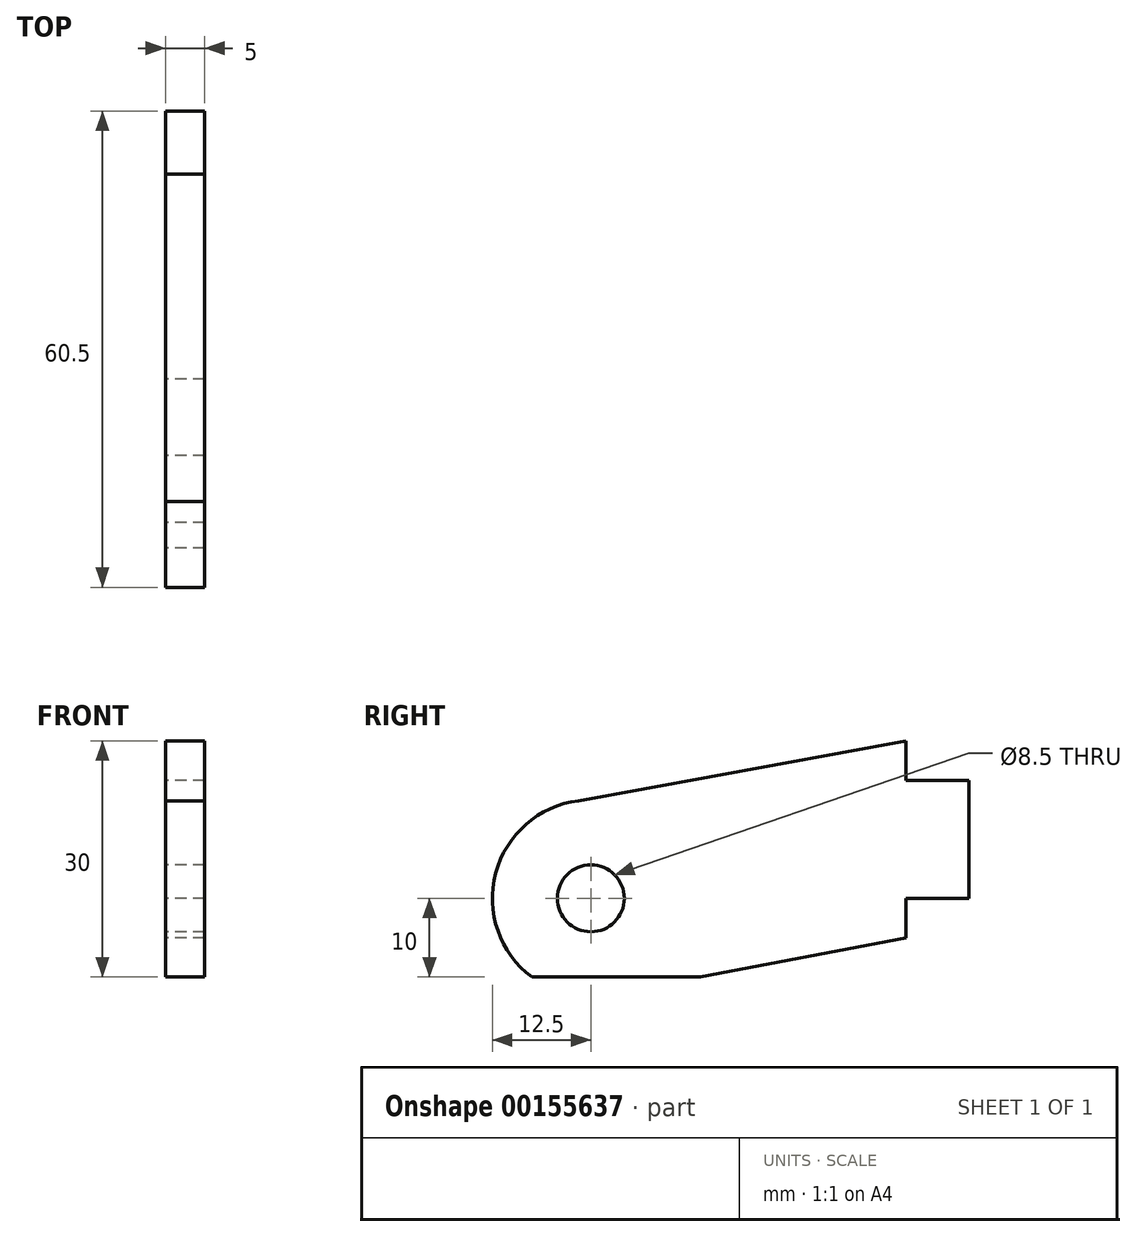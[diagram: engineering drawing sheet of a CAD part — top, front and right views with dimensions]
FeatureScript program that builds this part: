
annotation { "Feature Type Name" : "Feature", "Feature Type Description" : "" }
export const myFeature = defineFeature(function(context is Context, id is Id, definition is map)
    precondition{}
    {
        {
            var Q0;
            Q0=qCreatedBy(makeId("Right.planeOp"),FACE);
            var sketch = newSketch(context, id + "F0", { "sketchPlane" : qUnion([Q0])});
            skCircle(sketch, "E0", {"center": v(0, 0) * mm, "radius": 4.25 * mm});
            skArc(sketch, "E1", {"start": v(7.5, -10) * mm, "mid": v(0, 12.5) * mm, "end": v(-7.5, -10) * mm});
            skLineSegment(sketch, "E2", {"start": v(40, -5) * mm, "end": v(40, 20) * mm});
            skLineSegment(sketch, "E3", {"start": v(-7.5, -10) * mm, "end": v(13.96, -10) * mm});
            skLineSegment(sketch, "E4", {"start": v(40, 20) * mm, "end": v(-1.57, 12.4) * mm});
            skLineSegment(sketch, "E5", {"start": v(40, -5) * mm, "end": v(13.96, -10) * mm});
            skPoint(sketch, "E6.start.orphan", {"position": v(40, 15) * mm});
            skLineSegment(sketch, "E7.bottom", {"start": v(40, 15) * mm, "end": v(48, 15) * mm});
            skLineSegment(sketch, "E7.top", {"start": v(40, 0) * mm, "end": v(48, 0) * mm});
            skLineSegment(sketch, "E7.left", {"start": v(40, 15) * mm, "end": v(40, 0) * mm});
            skLineSegment(sketch, "E7.right", {"start": v(48, 15) * mm, "end": v(48, 0) * mm});
            skSolve(sketch);
        }
        {
            var Q0;
            {var subQ0=sQuery(id+"F0.wireOp",EDGE,"E6");Q0=makeQuery(id+"F0.imprint","IMPRINT",FACE,{"disambiguationData":[TD([[makeQuery(id+"F0.imprint","IMPRINT",EDGE,{"derivedFrom":subQ0}),-1.0]])]});}
            var Q1;
            Q1=makeQuery(id+"F0.imprint","IMPRINT",FACE,{"disambiguationData":[TD([[makeQuery(id+"F0.imprint","IMPRINT",EDGE,{"derivedFrom":sQuery(id+"F0.wireOp",EDGE,"E0")}),-1.0]])]});
            var Q2;
            {var subQ0=sQuery(id+"F0.wireOp",EDGE,"E4");Q2=makeQuery(id+"F0.imprint","IMPRINT",FACE,{"disambiguationData":[TD([[makeQuery(id+"F0.imprint","IMPRINT",EDGE,{"derivedFrom":subQ0}),1.0]])]});}
            var Q3;
            Q3=makeQuery(id+"F0.imprint","IMPRINT",FACE,{"disambiguationData":[TD([[makeQuery(id+"F0.imprint","IMPRINT",EDGE,{"derivedFrom":sQuery(id+"F0.wireOp",EDGE,"E7.bottom")}),-1.0]])]});
            extrude(context, id + "F1", {"entities" : qUnion([Q0, Q1, Q2, Q3]), "depth" : 5 * mm});
        }
    });
